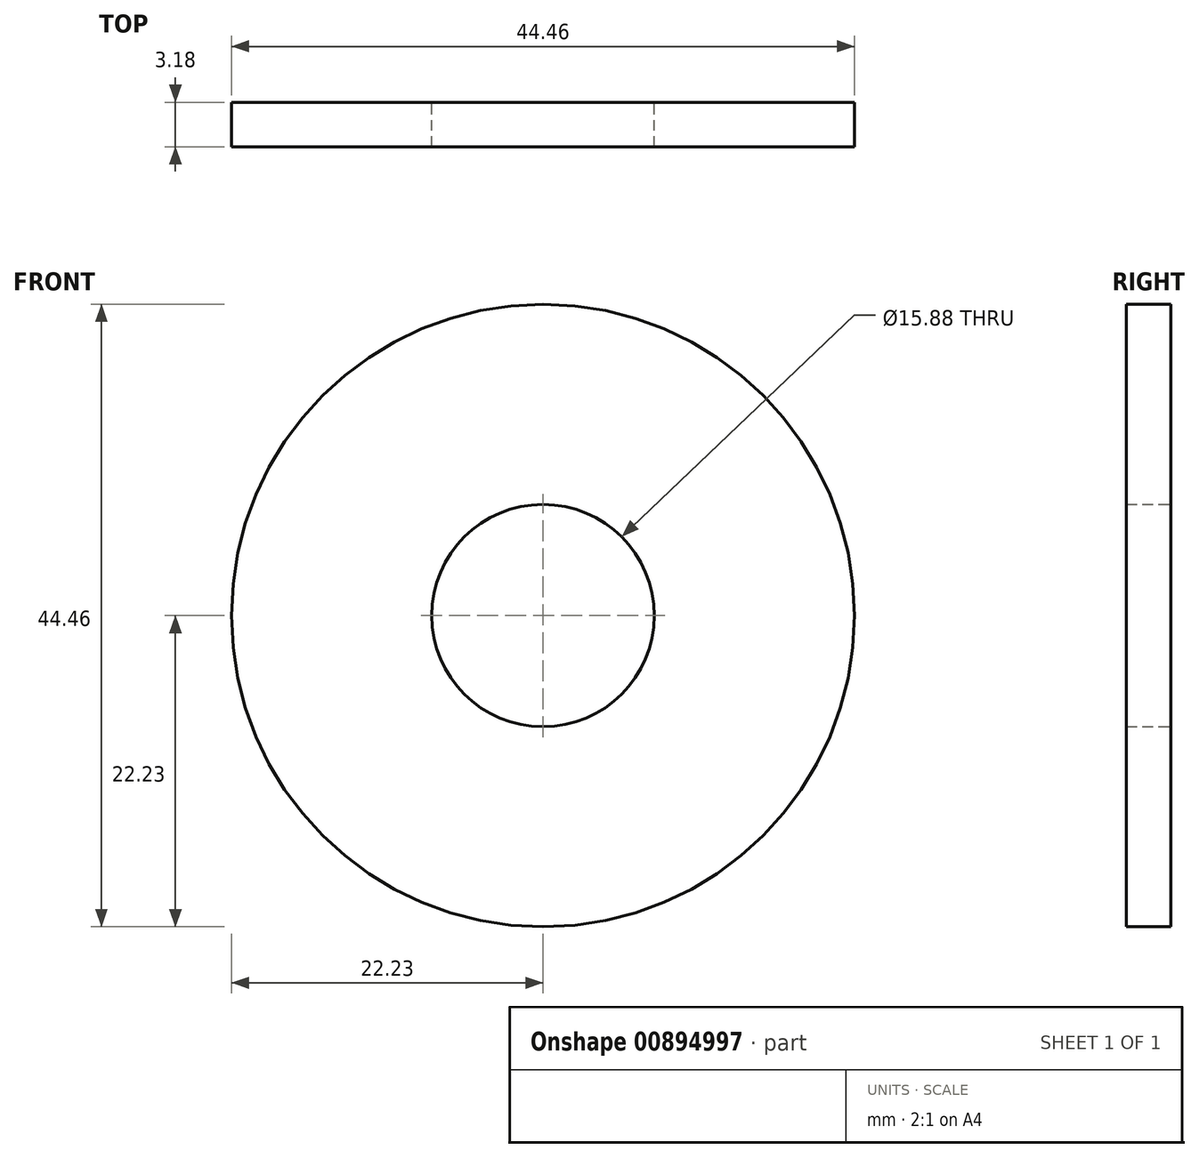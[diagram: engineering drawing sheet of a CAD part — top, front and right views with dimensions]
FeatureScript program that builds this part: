
annotation { "Feature Type Name" : "Feature", "Feature Type Description" : "" }
export const myFeature = defineFeature(function(context is Context, id is Id, definition is map)
    precondition{}
    {
        {
            var Q0;
            Q0=qCreatedBy(makeId("Front.planeOp"),FACE);
            var sketch = newSketch(context, id + "F0", { "sketchPlane" : qUnion([Q0])});
            skCircle(sketch, "E0", {"center": v(0, 0) * mm, "radius": 22.23 * mm});
            skCircle(sketch, "E1", {"center": v(0, 0) * mm, "radius": 7.94 * mm});
            skSolve(sketch);
        }
        {
            var Q0;
            Q0 = qSketchRegion(id + "F0", true);
            extrude(context, id + "F1", {"entities" : qUnion([Q0]), "depth" : 3.17 * mm, "offsetDistance" : 25.4 * mm});
        }
    });
